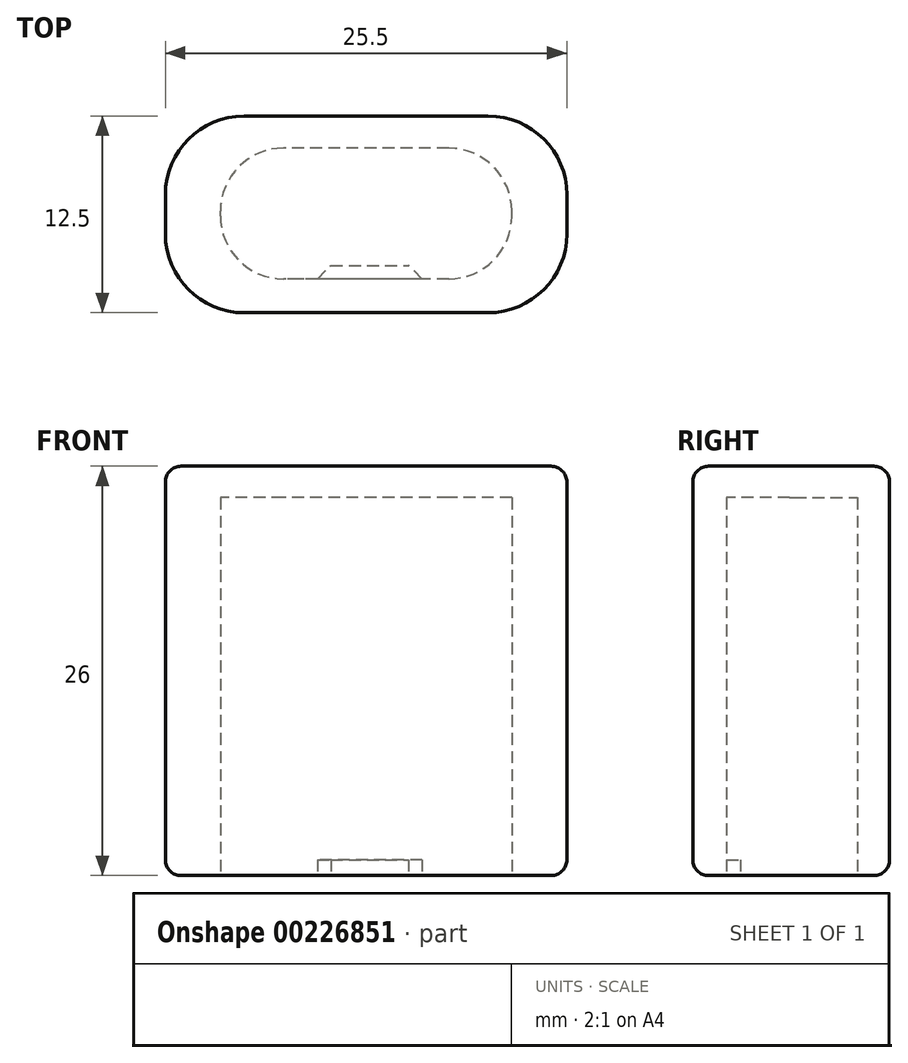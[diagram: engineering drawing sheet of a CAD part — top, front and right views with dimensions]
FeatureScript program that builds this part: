
annotation { "Feature Type Name" : "Feature", "Feature Type Description" : "" }
export const myFeature = defineFeature(function(context is Context, id is Id, definition is map)
    precondition{}
    {
        {
            var Q0;
            Q0=qCreatedBy(makeId("Top.planeOp"),FACE);
            var sketch = newSketch(context, id + "F0", { "sketchPlane" : qUnion([Q0])});
            skLineSegment(sketch, "E0.bottom", {"start": v(5.25, -5.48) * mm, "end": v(-5.25, -5.48) * mm});
            skLineSegment(sketch, "E0.top", {"start": v(5.25, 2.82) * mm, "end": v(-5.25, 2.82) * mm});
            skLineSegment(sketch, "E0.left", {"start": v(9.25, -1.48) * mm, "end": v(9.25, -1.18) * mm});
            skLineSegment(sketch, "E0.right", {"start": v(-9.25, -1.48) * mm, "end": v(-9.25, -1.18) * mm});
            skPoint(sketch, "E0.middle", {"position": v(0, -1.33) * mm});
            skPoint(sketch, "E1.visualSharp", {"position": v(9.25, -5.48) * mm});
            skArc(sketch, "E1.filletArc", {"start": v(5.25, -5.48) * mm, "mid": v(8.08, -4.3) * mm, "end": v(9.25, -1.48) * mm});
            skPoint(sketch, "E2.visualSharp", {"position": v(9.25, 2.82) * mm});
            skArc(sketch, "E2.filletArc", {"start": v(9.25, -1.18) * mm, "mid": v(8.08, 1.65) * mm, "end": v(5.25, 2.82) * mm});
            skPoint(sketch, "E3.visualSharp", {"position": v(-9.25, 2.82) * mm});
            skArc(sketch, "E3.filletArc", {"start": v(-5.25, 2.82) * mm, "mid": v(-8.08, 1.65) * mm, "end": v(-9.25, -1.18) * mm});
            skPoint(sketch, "E4.visualSharp", {"position": v(-9.25, -5.48) * mm});
            skArc(sketch, "E4.filletArc", {"start": v(-9.25, -1.48) * mm, "mid": v(-8.08, -4.3) * mm, "end": v(-5.25, -5.48) * mm});
            skSolve(sketch);
        }
        {
            var Q0;
            Q0=qCreatedBy(makeId("Top.planeOp"),FACE);
            var sketch = newSketch(context, id + "F1", { "sketchPlane" : qUnion([Q0])});
            skLineSegment(sketch, "E5.bottom", {"start": v(12.75, -7.63) * mm, "end": v(-12.75, -7.63) * mm});
            skLineSegment(sketch, "E5.top", {"start": v(12.75, 4.87) * mm, "end": v(-12.75, 4.87) * mm});
            skLineSegment(sketch, "E5.left", {"start": v(12.75, -7.63) * mm, "end": v(12.75, 4.87) * mm});
            skLineSegment(sketch, "E5.right", {"start": v(-12.75, -7.63) * mm, "end": v(-12.75, 4.87) * mm});
            skPoint(sketch, "E5.middle", {"position": v(0, -1.38) * mm});
            skSolve(sketch);
        }
        {
            var Q0;
            Q0=makeQuery(id+"F1.imprint","IMPRINT",FACE,{"disambiguationData":[TD([[makeQuery(id+"F1.imprint","IMPRINT",EDGE,{"derivedFrom":sQuery(id+"F1.wireOp",EDGE,"E5.bottom")}),-1.0]])]});
            extrude(context, id + "F2", {"entities" : qUnion([Q0]), "depth" : 26 * mm});
        }
        {
            var Q0;
            {var subQ4=sQuery(id+"F0.wireOp",EDGE,"E0.bottom");Q0=makeQuery(id+"F0.imprint","IMPRINT",FACE,{"disambiguationData":[TD([[makeQuery(id+"F0.imprint","IMPRINT",EDGE,{"derivedFrom":subQ4}),-1.0]])]});}
            extrude(context, id + "F3", {"entities" : qUnion([Q0]), "operationType" : NewBodyOperationType.REMOVE, "depth" : 24 * mm});
        }
        {
            var Q0;
            Q0=makeQuery(id+"F2.opExtrude","SWEPT_EDGE",EDGE,{"disambiguationData":[OSD([sQuery(id+"F1.wireOp",EDGE,"E5.bottom"),sQuery(id+"F1.wireOp",EDGE,"E5.left")])]});
            var Q1;
            Q1=makeQuery(id+"F2.opExtrude","SWEPT_EDGE",EDGE,{"disambiguationData":[OSD([sQuery(id+"F1.wireOp",EDGE,"E5.top"),sQuery(id+"F1.wireOp",EDGE,"E5.left")])]});
            var Q2;
            Q2=makeQuery(id+"F2.opExtrude","SWEPT_EDGE",EDGE,{"disambiguationData":[OSD([sQuery(id+"F1.wireOp",EDGE,"E5.bottom"),sQuery(id+"F1.wireOp",EDGE,"E5.right")])]});
            var Q3;
            Q3=makeQuery(id+"F2.opExtrude","SWEPT_EDGE",EDGE,{"disambiguationData":[OSD([sQuery(id+"F1.wireOp",EDGE,"E5.top"),sQuery(id+"F1.wireOp",EDGE,"E5.right")])]});
            fillet(context, id + "F4", {"entities" : qUnion([Q0, Q1, Q2, Q3]), "radius" : 5 * mm, "tangentPropagation" : true, "allowEdgeOverflow" : false});
        }
        {
            var Q0;
            Q0=makeQuery(id+"F2.opExtrude","CAP_EDGE",EDGE,{"disambiguationData":[OSD([sQuery(id+"F1.wireOp",EDGE,"E5.top")])],"isStart":true});
            var Q1;
            Q1=makeQuery(id+"F2.opExtrude","CAP_EDGE",EDGE,{"disambiguationData":[OSD([sQuery(id+"F1.wireOp",EDGE,"E5.top")])],"isStart":false});
            fillet(context, id + "F5", {"entities" : qUnion([Q0, Q1]), "radius" : 1 * mm, "tangentPropagation" : true, "allowEdgeOverflow" : false});
        }
        {
            var Q0;
            Q0=makeQuery(id+"F1.imprint","IMPRINT",FACE,{"disambiguationData":[TD([[makeQuery(id+"F1.imprint","IMPRINT",EDGE,{"derivedFrom":sQuery(id+"F1.wireOp",EDGE,"E5.bottom")}),-1.0]])]});
            var sketch = newSketch(context, id + "F6", { "sketchPlane" : qUnion([Q0])});
            skLineSegment(sketch, "E6.bottom", {"start": v(-3.12, -5.5) * mm, "end": v(3.59, -5.5) * mm});
            skLineSegment(sketch, "E6.top", {"start": v(-2.24, -4.62) * mm, "end": v(2.7, -4.62) * mm});
            skLineSegment(sketch, "E7", {"start": v(-3.12, -5.5) * mm, "end": v(-2.24, -4.62) * mm});
            skLineSegment(sketch, "E8", {"start": v(3.59, -5.5) * mm, "end": v(2.7, -4.62) * mm});
            skSolve(sketch);
        }
        {
            var Q0;
            Q0 = qSketchRegion(id + "F6", true);
            extrude(context, id + "F7", {"entities" : qUnion([Q0]), "operationType" : NewBodyOperationType.ADD, "depth" : 1 * mm});
        }
    });
